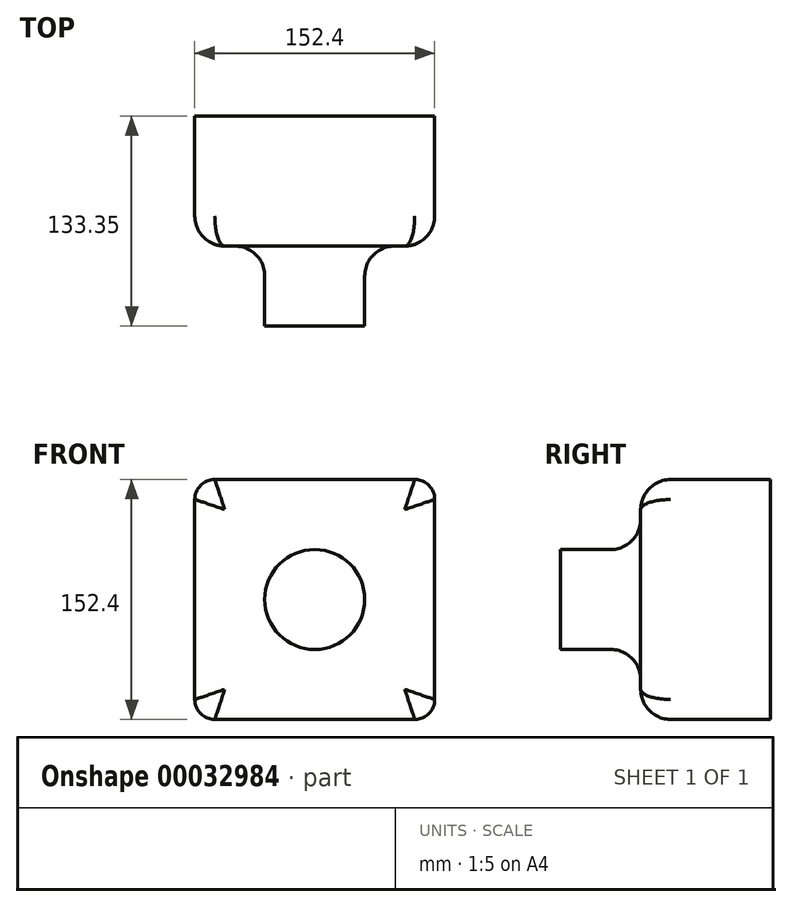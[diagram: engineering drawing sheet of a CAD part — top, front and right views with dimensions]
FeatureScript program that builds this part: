
annotation { "Feature Type Name" : "Feature", "Feature Type Description" : "" }
export const myFeature = defineFeature(function(context is Context, id is Id, definition is map)
    precondition{}
    {
        {
            var Q0;
            Q0=qCreatedBy(makeId("Front.planeOp"),FACE);
            var sketch = newSketch(context, id + "F0", { "sketchPlane" : qUnion([Q0])});
            skLineSegment(sketch, "E0.rect.bottom", {"start": v(76.2, 76.2) * mm, "end": v(-76.2, 76.2) * mm});
            skLineSegment(sketch, "E0.rect.top", {"start": v(76.2, -76.2) * mm, "end": v(-76.2, -76.2) * mm});
            skLineSegment(sketch, "E0.rect.left", {"start": v(76.2, 76.2) * mm, "end": v(76.2, -76.2) * mm});
            skLineSegment(sketch, "E0.rect.right", {"start": v(-76.2, 76.2) * mm, "end": v(-76.2, -76.2) * mm});
            skPoint(sketch, "E0.rect.middle", {"position": v(0, 0) * mm});
            skSolve(sketch);
        }
        {
            var Q0;
            Q0 = qSketchRegion(id + "F0", true);
            extrude(context, id + "F1", {"entities" : qUnion([Q0]), "depth" : 82.55 * mm});
        }
        {
            var Q0;
            Q0=makeQuery(id+"F1.opExtrude","CAP_FACE",FACE,{"disambiguationData":[OSD([sQuery(id+"F0.wireOp",EDGE,"E0.rect.bottom"),sQuery(id+"F0.wireOp",EDGE,"E0.rect.top"),sQuery(id+"F0.wireOp",EDGE,"E0.rect.left"),sQuery(id+"F0.wireOp",EDGE,"E0.rect.right")])],"isStart":false});
            var sketch = newSketch(context, id + "F2", { "sketchPlane" : qUnion([Q0])});
            skCircle(sketch, "E1", {"center": v(0, 0) * mm, "radius": 31.75 * mm});
            skSolve(sketch);
        }
        {
            var Q0;
            Q0 = qSketchRegion(id + "F2", true);
            extrude(context, id + "F3", {"entities" : qUnion([Q0]), "operationType" : NewBodyOperationType.ADD, "depth" : 50.8 * mm});
        }
        {
            var Q0;
            Q0=makeQuery(id+"F1.opExtrude","SWEPT_EDGE",EDGE,{"disambiguationData":[OSD([sQuery(id+"F0.wireOp",EDGE,"E0.rect.bottom"),sQuery(id+"F0.wireOp",EDGE,"E0.rect.right")])]});
            var Q1;
            Q1=makeQuery(id+"F1.opExtrude","SWEPT_EDGE",EDGE,{"disambiguationData":[OSD([sQuery(id+"F0.wireOp",EDGE,"E0.rect.bottom"),sQuery(id+"F0.wireOp",EDGE,"E0.rect.left")])]});
            var Q2;
            Q2=makeQuery(id+"F1.opExtrude","SWEPT_EDGE",EDGE,{"disambiguationData":[OSD([sQuery(id+"F0.wireOp",EDGE,"E0.rect.top"),sQuery(id+"F0.wireOp",EDGE,"E0.rect.left")])]});
            var Q3;
            Q3=makeQuery(id+"F1.opExtrude","SWEPT_EDGE",EDGE,{"disambiguationData":[OSD([sQuery(id+"F0.wireOp",EDGE,"E0.rect.top"),sQuery(id+"F0.wireOp",EDGE,"E0.rect.right")])]});
            fillet(context, id + "F4", {"entities" : qUnion([Q0, Q1, Q2, Q3]), "radius" : 12.7 * mm, "tangentPropagation" : true, "allowEdgeOverflow" : false});
        }
        {
            var Q0;
            Q0=makeQuery(id+"F1.opExtrude","CAP_FACE",FACE,{"disambiguationData":[OSD([sQuery(id+"F0.wireOp",EDGE,"E0.rect.bottom"),sQuery(id+"F0.wireOp",EDGE,"E0.rect.top"),sQuery(id+"F0.wireOp",EDGE,"E0.rect.left"),sQuery(id+"F0.wireOp",EDGE,"E0.rect.right")])],"isStart":false});
            fillet(context, id + "F5", {"entities" : qUnion([Q0]), "radius" : 19.05 * mm, "tangentPropagation" : true, "allowEdgeOverflow" : false});
        }
    });
